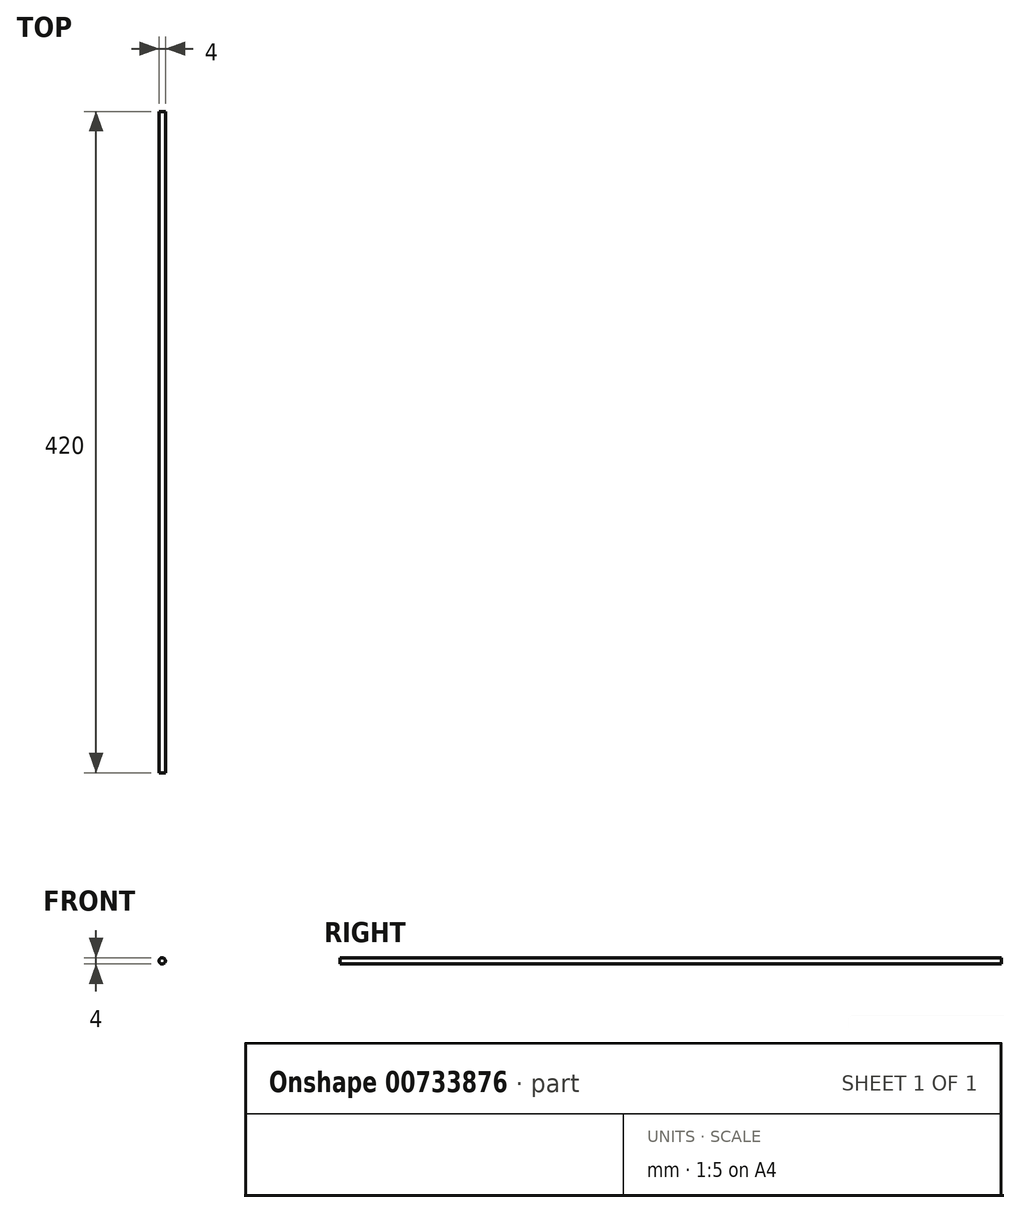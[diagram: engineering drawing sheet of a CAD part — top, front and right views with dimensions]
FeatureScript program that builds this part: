
annotation { "Feature Type Name" : "Feature", "Feature Type Description" : "" }
export const myFeature = defineFeature(function(context is Context, id is Id, definition is map)
    precondition{}
    {
        {
            var Q0;
            Q0=qCreatedBy(makeId("Front.planeOp"),FACE);
            var sketch = newSketch(context, id + "F0", { "sketchPlane" : qUnion([Q0])});
            skCircle(sketch, "E0", {"center": v(0, 0) * mm, "radius": 2 * mm});
            skSolve(sketch);
        }
        {
            var Q0;
            Q0=makeQuery(id+"F0.imprint","IMPRINT",FACE,{"disambiguationData":[TD([[makeQuery(id+"F0.imprint","IMPRINT",EDGE,{"derivedFrom":sQuery(id+"F0.wireOp",EDGE,"E0")}),1.0]])]});
            extrude(context, id + "F1", {"entities" : qUnion([Q0]), "depth" : 420 * mm, "offsetDistance" : 25 * mm});
        }
    });
